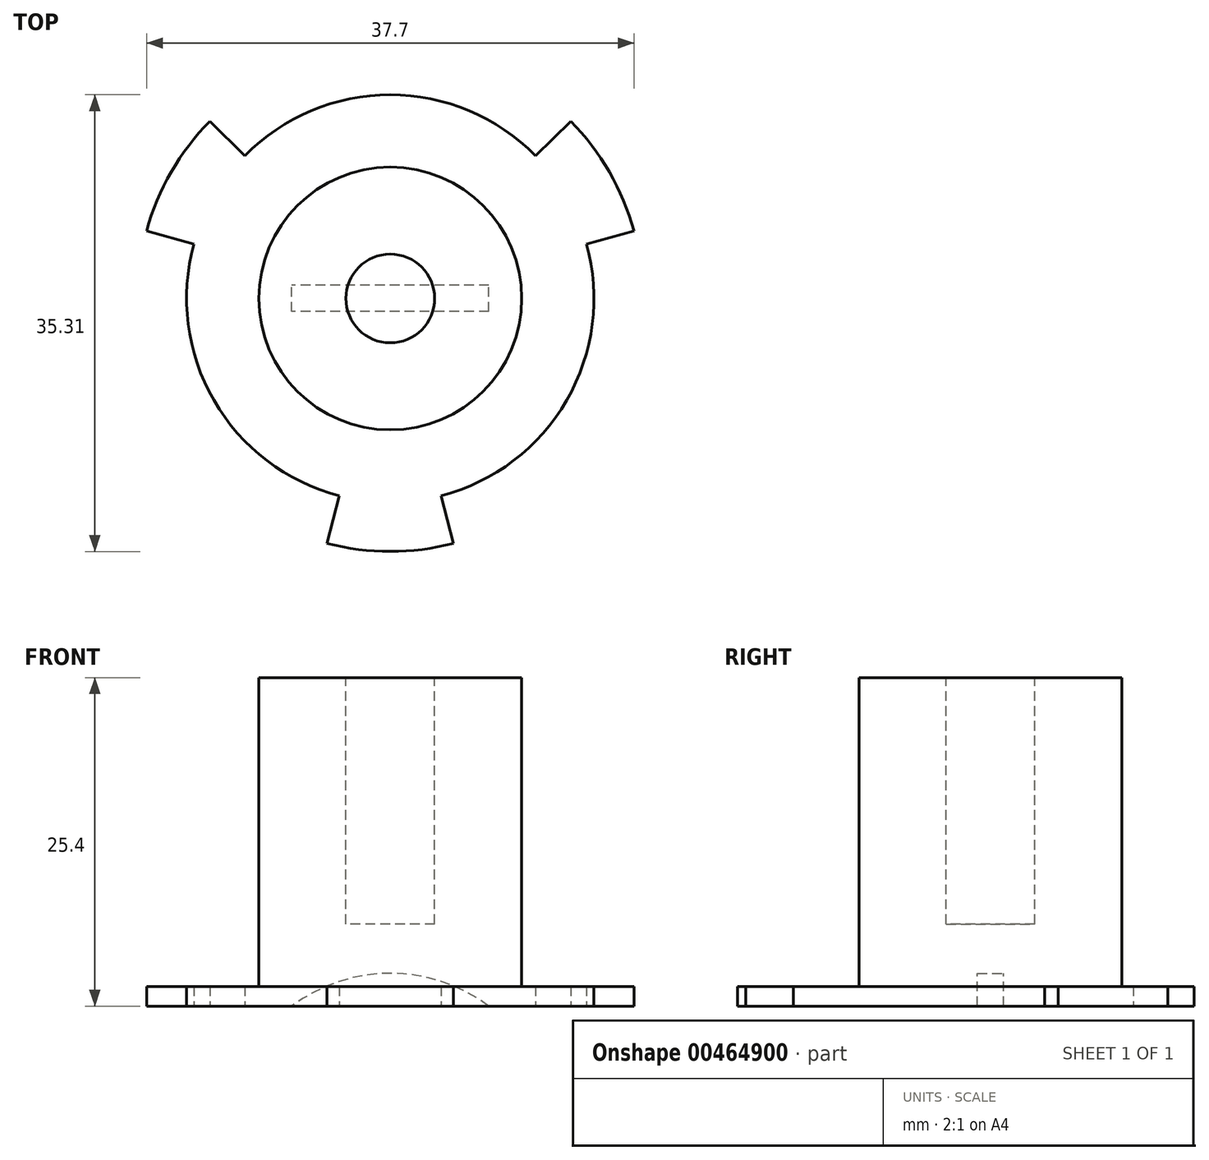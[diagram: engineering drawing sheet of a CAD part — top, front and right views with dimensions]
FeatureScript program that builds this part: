
annotation { "Feature Type Name" : "Feature", "Feature Type Description" : "" }
export const myFeature = defineFeature(function(context is Context, id is Id, definition is map)
    precondition{}
    {
        {
            var Q0;
            Q0=qCreatedBy(makeId("Front.planeOp"),FACE);
            var sketch = newSketch(context, id + "F0", { "sketchPlane" : qUnion([Q0])});
            skLineSegment(sketch, "E0", {"start": v(0, 0) * mm, "end": v(0, 25.4) * mm});
            skLineSegment(sketch, "E1", {"start": v(0, 25.4) * mm, "end": v(10.16, 25.4) * mm});
            skLineSegment(sketch, "E2", {"start": v(10.16, 25.4) * mm, "end": v(10.16, 1.52) * mm});
            skLineSegment(sketch, "E3", {"start": v(10.16, 1.52) * mm, "end": v(19.56, 1.52) * mm});
            skLineSegment(sketch, "E4", {"start": v(19.56, 1.52) * mm, "end": v(19.56, 0) * mm});
            skLineSegment(sketch, "E5", {"start": v(19.56, 0) * mm, "end": v(0, 0) * mm});
            skLineSegment(sketch, "E6", {"start": v(0, 29.12) * mm, "end": v(0, -8.28) * mm, "construction": true});
            skSolve(sketch);
        }
        {
            var Q0;
            Q0=makeQuery(id+"F0.imprint","IMPRINT",FACE,{"disambiguationData":[TD([[makeQuery(id+"F0.imprint","IMPRINT",EDGE,{"derivedFrom":sQuery(id+"F0.wireOp",EDGE,"E0")}),-1.0]])]});
            var Q1;
            Q1=sQuery(id+"F0.wireOp",EDGE,"E6");
            revolve(context, id + "F1", {"entities" : qUnion([Q0]), "axis" : qUnion([Q1]), "revolveType" : RevolveType.FULL});
        }
        {
            var Q0;
            Q0=makeQuery(id+"F1.opRevolve","SWEPT_FACE",FACE,{"disambiguationData":[OSD([sQuery(id+"F0.wireOp",EDGE,"E5")])]});
            var sketch = newSketch(context, id + "F2", { "sketchPlane" : qUnion([Q0])});
            skLineSegment(sketch, "E7", {"start": v(3.94, 15.25) * mm, "end": v(4.9, 18.94) * mm});
            skLineSegment(sketch, "E8", {"start": v(-3.94, 15.25) * mm, "end": v(-4.9, 18.94) * mm});
            skLineSegment(sketch, "E9", {"start": v(0, 0) * mm, "end": v(16.94, -9.78) * mm, "construction": true});
            skLineSegment(sketch, "E10", {"start": v(0, 0) * mm, "end": v(-16.94, -9.78) * mm, "construction": true});
            skLineSegment(sketch, "E11", {"start": v(0, 0) * mm, "end": v(0, 18.36) * mm});
            skLineSegment(sketch, "E12", {"start": v(15.18, -4.2) * mm, "end": v(18.85, -5.23) * mm});
            skLineSegment(sketch, "E13", {"start": v(11.23, -11.04) * mm, "end": v(13.95, -13.7) * mm});
            skLineSegment(sketch, "E14", {"start": v(-11.23, -11.04) * mm, "end": v(-13.95, -13.7) * mm});
            skLineSegment(sketch, "E15", {"start": v(-15.18, -4.2) * mm, "end": v(-18.85, -5.23) * mm});
            skArc(sketch, "E16", {"start": v(-3.94, 15.25) * mm, "mid": v(-13.64, 7.87) * mm, "end": v(-15.18, -4.2) * mm});
            skArc(sketch, "E17.trimOffspring", {"start": v(-11.23, -11.04) * mm, "mid": v(0, -15.75) * mm, "end": v(11.23, -11.04) * mm});
            skArc(sketch, "E18.trimOffspring", {"start": v(15.18, -4.2) * mm, "mid": v(13.64, 7.87) * mm, "end": v(3.94, 15.25) * mm});
            skArc(sketch, "E19.0", {"start": v(-13.95, -13.7) * mm, "mid": v(0, -19.56) * mm, "end": v(13.95, -13.7) * mm});
            skArc(sketch, "E20.trimOffspring", {"start": v(18.85, -5.23) * mm, "mid": v(16.94, 9.78) * mm, "end": v(4.9, 18.94) * mm});
            skArc(sketch, "E21.trimOffspring", {"start": v(-4.9, 18.94) * mm, "mid": v(-16.94, 9.78) * mm, "end": v(-18.85, -5.23) * mm});
            skSolve(sketch);
        }
        {
            var Q0;
            Q0=makeQuery(id+"F2.imprint","IMPRINT",FACE,{"disambiguationData":[TD([[makeQuery(id+"F2.imprint","IMPRINT",EDGE,{"derivedFrom":sQuery(id+"F2.wireOp",EDGE,"E8")}),1.0]])]});
            var Q1;
            Q1=makeQuery(id+"F2.imprint","IMPRINT",FACE,{"disambiguationData":[TD([[makeQuery(id+"F2.imprint","IMPRINT",EDGE,{"derivedFrom":sQuery(id+"F2.wireOp",EDGE,"E7")}),-1.0]])]});
            var Q2;
            Q2=makeQuery(id+"F2.imprint","IMPRINT",FACE,{"disambiguationData":[TD([[makeQuery(id+"F2.imprint","IMPRINT",EDGE,{"derivedFrom":sQuery(id+"F2.wireOp",EDGE,"E13")}),-1.0]])]});
            extrude(context, id + "F3", {"entities" : qUnion([Q0, Q1, Q2]), "operationType" : NewBodyOperationType.REMOVE, "endBound" : BoundingType.THROUGH_ALL, "oppositeDirection" : true, "depth" : 25.4 * mm});
        }
        {
            var Q0;
            Q0=makeQuery(id+"F1.opRevolve","SWEPT_FACE",FACE,{"disambiguationData":[OSD([sQuery(id+"F0.wireOp",EDGE,"E1")])]});
            var sketch = newSketch(context, id + "F4", { "sketchPlane" : qUnion([Q0])});
            skCircle(sketch, "E22", {"center": v(0, 0) * mm, "radius": 3.43 * mm});
            skSolve(sketch);
        }
        {
            var Q0;
            Q0=makeQuery(id+"F4.imprint","IMPRINT",FACE,{"disambiguationData":[TD([[makeQuery(id+"F4.imprint","IMPRINT",EDGE,{"derivedFrom":sQuery(id+"F4.wireOp",EDGE,"E22")}),1.0]])]});
            extrude(context, id + "F5", {"entities" : qUnion([Q0]), "operationType" : NewBodyOperationType.REMOVE, "oppositeDirection" : true, "depth" : 19.05 * mm});
        }
        {
            var Q0;
            Q0=qCreatedBy(makeId("Front.planeOp"),FACE);
            var sketch = newSketch(context, id + "F6", { "sketchPlane" : qUnion([Q0])});
            skCircle(sketch, "E23", {"center": v(0, -10.16) * mm, "radius": 12.7 * mm});
            skSolve(sketch);
        }
        {
            var Q0;
            Q0=makeQuery(id+"F6.imprint","IMPRINT",FACE,{"disambiguationData":[TD([[makeQuery(id+"F6.imprint","IMPRINT",EDGE,{"derivedFrom":sQuery(id+"F6.wireOp",EDGE,"E23")}),1.0]])]});
            var Q1;
            Q1 = qConstructionFilter(qBodyType(qCreatedBy(id + "F6" ,EDGE), BodyType.WIRE), ConstructionObject.NO);
            extrude(context, id + "F7", {"entities" : qUnion([Q0]), "operationType" : NewBodyOperationType.REMOVE, "surfaceEntities" : qUnion([Q1]), "endBound" : BoundingType.SYMMETRIC, "depth" : 2.03 * mm});
        }
    });
